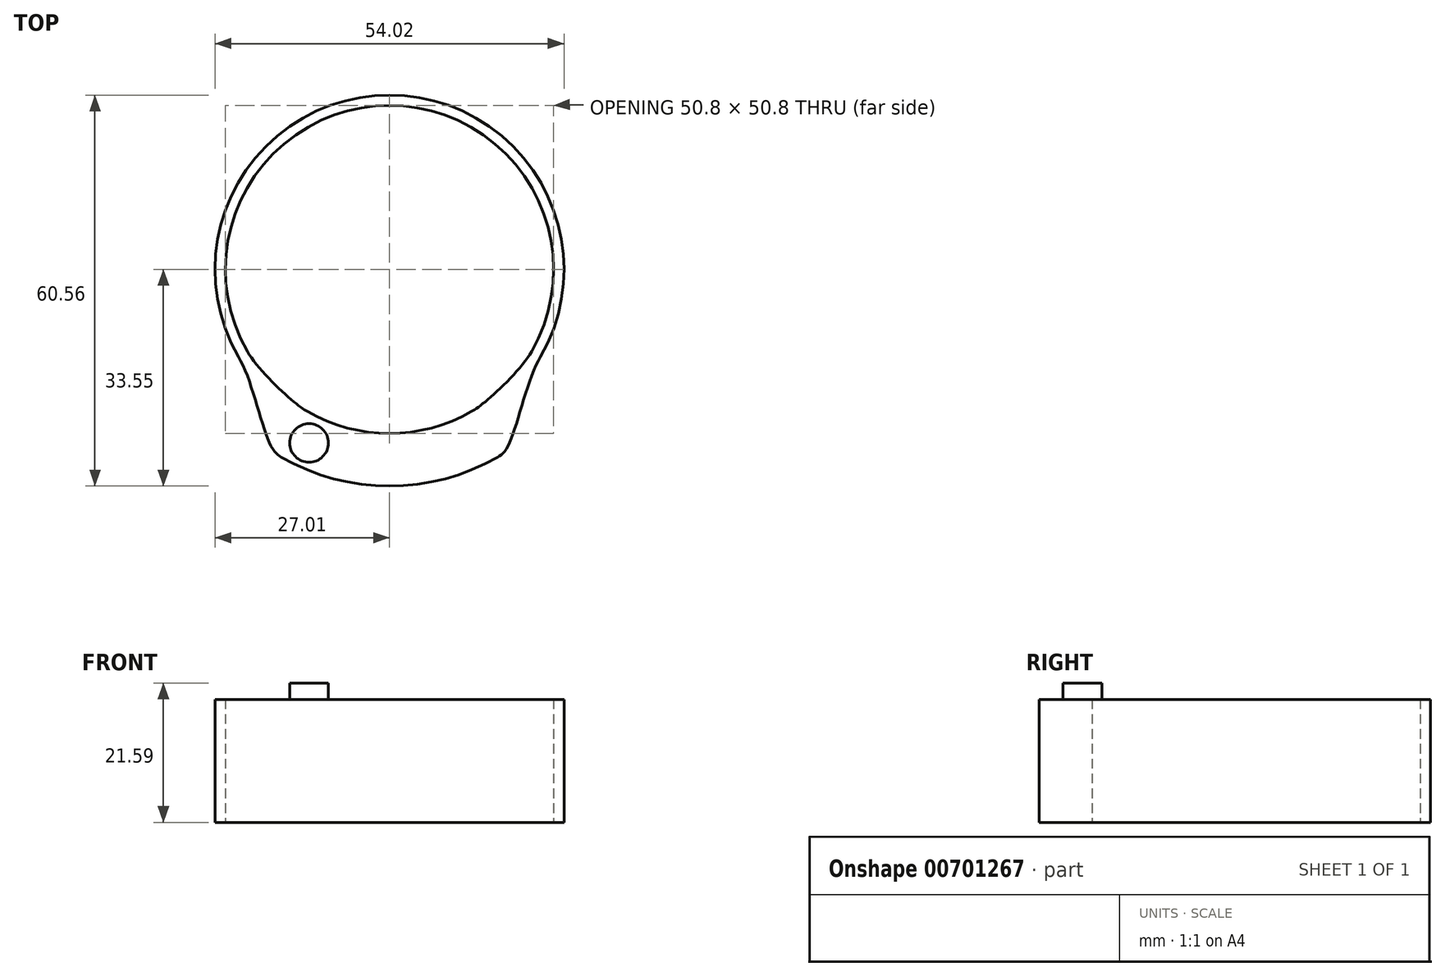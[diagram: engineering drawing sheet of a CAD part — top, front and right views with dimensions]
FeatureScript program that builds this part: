
annotation { "Feature Type Name" : "Feature", "Feature Type Description" : "" }
export const myFeature = defineFeature(function(context is Context, id is Id, definition is map)
    precondition{}
    {
        {
            var Q0;
            Q0=qCreatedBy(makeId("Front.planeOp"),FACE);
            var sketch = newSketch(context, id + "F0", { "sketchPlane" : qUnion([Q0])});
            skLineSegment(sketch, "E0.bottom", {"start": v(25.4, 0) * mm, "end": v(27, 0) * mm});
            skLineSegment(sketch, "E0.top", {"start": v(25.4, 19.05) * mm, "end": v(27, 19.05) * mm});
            skLineSegment(sketch, "E0.left", {"start": v(25.4, 0) * mm, "end": v(25.4, 19.05) * mm});
            skLineSegment(sketch, "E0.right", {"start": v(27, 0) * mm, "end": v(27, 19.05) * mm});
            skSolve(sketch);
        }
        {
            var Q0;
            Q0=qCreatedBy(makeId("Front.planeOp"),FACE);
            var sketch = newSketch(context, id + "F1", { "sketchPlane" : qUnion([Q0])});
            skLineSegment(sketch, "E1", {"start": v(0, 0) * mm, "end": v(0, 61.6) * mm});
            skSolve(sketch);
        }
        {
            var Q0;
            Q0=qSketchRegion(id+"F0",true);
            var Q1;
            Q1=sQuery(id+"F1.wireOp",EDGE,"E1");
            revolve(context, id + "F2", {"entities" : qUnion([Q0]), "axis" : qUnion([Q1]), "revolveType" : RevolveType.TWO_DIRECTIONS, "angle" : 210 * degree, "angleBack" : 330 * degree});
        }
        {
            var Q0;
            Q0=qCreatedBy(makeId("Right.planeOp"),FACE);
            var sketch = newSketch(context, id + "F3", { "sketchPlane" : qUnion([Q0])});
            skLineSegment(sketch, "E2.bottom", {"start": v(-25.4, 0) * mm, "end": v(-33.55, 0) * mm});
            skLineSegment(sketch, "E2.top", {"start": v(-25.4, 19.05) * mm, "end": v(-33.55, 19.05) * mm});
            skLineSegment(sketch, "E2.left", {"start": v(-25.4, 0) * mm, "end": v(-25.4, 19.05) * mm});
            skLineSegment(sketch, "E2.right", {"start": v(-33.55, 0) * mm, "end": v(-33.55, 19.05) * mm});
            skSolve(sketch);
        }
        {
            var Q0;
            Q0=qSketchRegion(id+"F3",true);
            var Q1;
            Q1=sQuery(id+"F1.wireOp",EDGE,"E1");
            revolve(context, id + "F4", {"entities" : qUnion([Q0]), "axis" : qUnion([Q1]), "revolveType" : RevolveType.TWO_DIRECTIONS, "angle" : 30 * degree, "angleBack" : 330 * degree});
        }
        {
            var Q0;
            Q0=makeQuery(id+"F4.opRevolve","CAP_FACE",FACE,{"disambiguationData":[OSD([sQuery(id+"F3.wireOp",EDGE,"E2.bottom"),sQuery(id+"F3.wireOp",EDGE,"E2.top"),sQuery(id+"F3.wireOp",EDGE,"E2.left"),sQuery(id+"F3.wireOp",EDGE,"E2.right")])],"isStart":true});
            var Q1;
            Q1=makeQuery(id+"F2.opRevolve","CAP_FACE",FACE,{"disambiguationData":[OSD([sQuery(id+"F0.wireOp",EDGE,"E0.bottom"),sQuery(id+"F0.wireOp",EDGE,"E0.top"),sQuery(id+"F0.wireOp",EDGE,"E0.left"),sQuery(id+"F0.wireOp",EDGE,"E0.right")])],"isStart":false});
            loft(context, id + "F5", {"operationType" : NewBodyOperationType.ADD, "startCondition" : LoftEndDerivativeType.MATCH_CURVATURE, "startMagnitude" : .5, "endCondition" : LoftEndDerivativeType.MATCH_TANGENT, "endMagnitude" : 1, "sheetProfilesArray" : [{ "sheetProfileEntities" : qUnion([Q0]) }, { "sheetProfileEntities" : qUnion([Q1]) }]});
        }
        {
            var Q1;
            Q1=makeQuery(id+"F4.opRevolve","CAP_FACE",FACE,{"disambiguationData":[OSD([sQuery(id+"F3.wireOp",EDGE,"E2.bottom"),sQuery(id+"F3.wireOp",EDGE,"E2.top"),sQuery(id+"F3.wireOp",EDGE,"E2.left"),sQuery(id+"F3.wireOp",EDGE,"E2.right")])],"isStart":false});
            var Q2;
            Q2=makeQuery(id+"F2.opRevolve","CAP_FACE",FACE,{"disambiguationData":[OSD([sQuery(id+"F0.wireOp",EDGE,"E0.bottom"),sQuery(id+"F0.wireOp",EDGE,"E0.top"),sQuery(id+"F0.wireOp",EDGE,"E0.left"),sQuery(id+"F0.wireOp",EDGE,"E0.right")])],"isStart":true});
            loft(context, id + "F6", {"operationType" : NewBodyOperationType.ADD, "startCondition" : LoftEndDerivativeType.MATCH_CURVATURE, "startMagnitude" : .5, "endCondition" : LoftEndDerivativeType.MATCH_TANGENT, "endMagnitude" : 1, "sheetProfilesArray" : [{ "sheetProfileEntities" : qUnion([Q1]) }, { "sheetProfileEntities" : qUnion([Q2]) }]});
        }
        {
            var Q0;
            {var subQ0=sQuery(id+"F3.wireOp",EDGE,"E2.right");var subQ1=sQuery(id+"F3.wireOp",EDGE,"E2.left");var subQ2=sQuery(id+"F3.wireOp",EDGE,"E2.top");var subQ3=sQuery(id+"F0.wireOp",EDGE,"E0.right");var subQ4=sQuery(id+"F0.wireOp",EDGE,"E0.left");var subQ5=sQuery(id+"F0.wireOp",EDGE,"E0.top");Q0=makeQuery(id+"F6.boolean.opBoolean","MERGE",FACE,{"derivedFrom":[makeQuery(id+"F5.boolean.opBoolean","MERGE",FACE,{"derivedFrom":[makeQuery(id+"F2.opRevolve","SWEPT_FACE",FACE,{"disambiguationData":[OSD([subQ5])]}),makeQuery(id+"F4.opRevolve","SWEPT_FACE",FACE,{"disambiguationData":[OSD([subQ2])]}),makeQuery(id+"F5.opLoft","SWEPT_FACE",FACE,{"disambiguationData":[OSD([subQ5,subQ4,subQ3,subQ2,subQ1,subQ0])]})]}),makeQuery(id+"F6.opLoft","SWEPT_FACE",FACE,{"disambiguationData":[OSD([subQ5,subQ4,subQ3,subQ2,subQ1,subQ0])]})]});}
            var sketch = newSketch(context, id + "F7", { "sketchPlane" : qUnion([Q0])});
            skCircle(sketch, "E3", {"center": v(-12.45, -26.87) * mm, "radius": 3 * mm});
            skSolve(sketch);
        }
        {
            var Q0;
            Q0=qSketchRegion(id+"F7",true);
            extrude(context, id + "F8", {"entities" : qUnion([Q0]), "operationType" : NewBodyOperationType.ADD, "depth" : 2.54 * mm, "offsetDistance" : 25.4 * mm});
        }
    });
